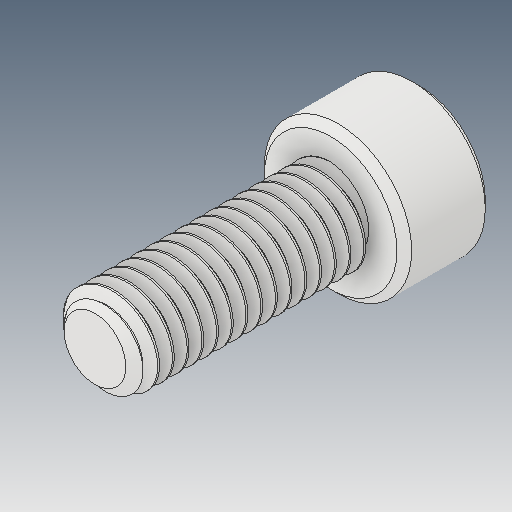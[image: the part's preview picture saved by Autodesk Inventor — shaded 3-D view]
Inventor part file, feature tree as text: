
AUTODESK INVENTOR PART (.ipt)
format: ipt  version: 2019 (Build 230136000, 136)  size: 678,400 bytes
history: native  units: mm
features: chamfer x1
ambient origin geometry x8: Origin, YZ Plane, XZ Plane, XY Plane, X Axis, Y Axis, Z Axis, Center Point
bodies: Solid1 (feature_tree)
feature tree (1):
  chamfer  "Chamfer1"  [1 undecoded]
note: 1 required parameter value undecoded (feature->parameter linkage not recoverable at this tier; creation-order binding heuristic only, values carry confidence <= 0.55)
